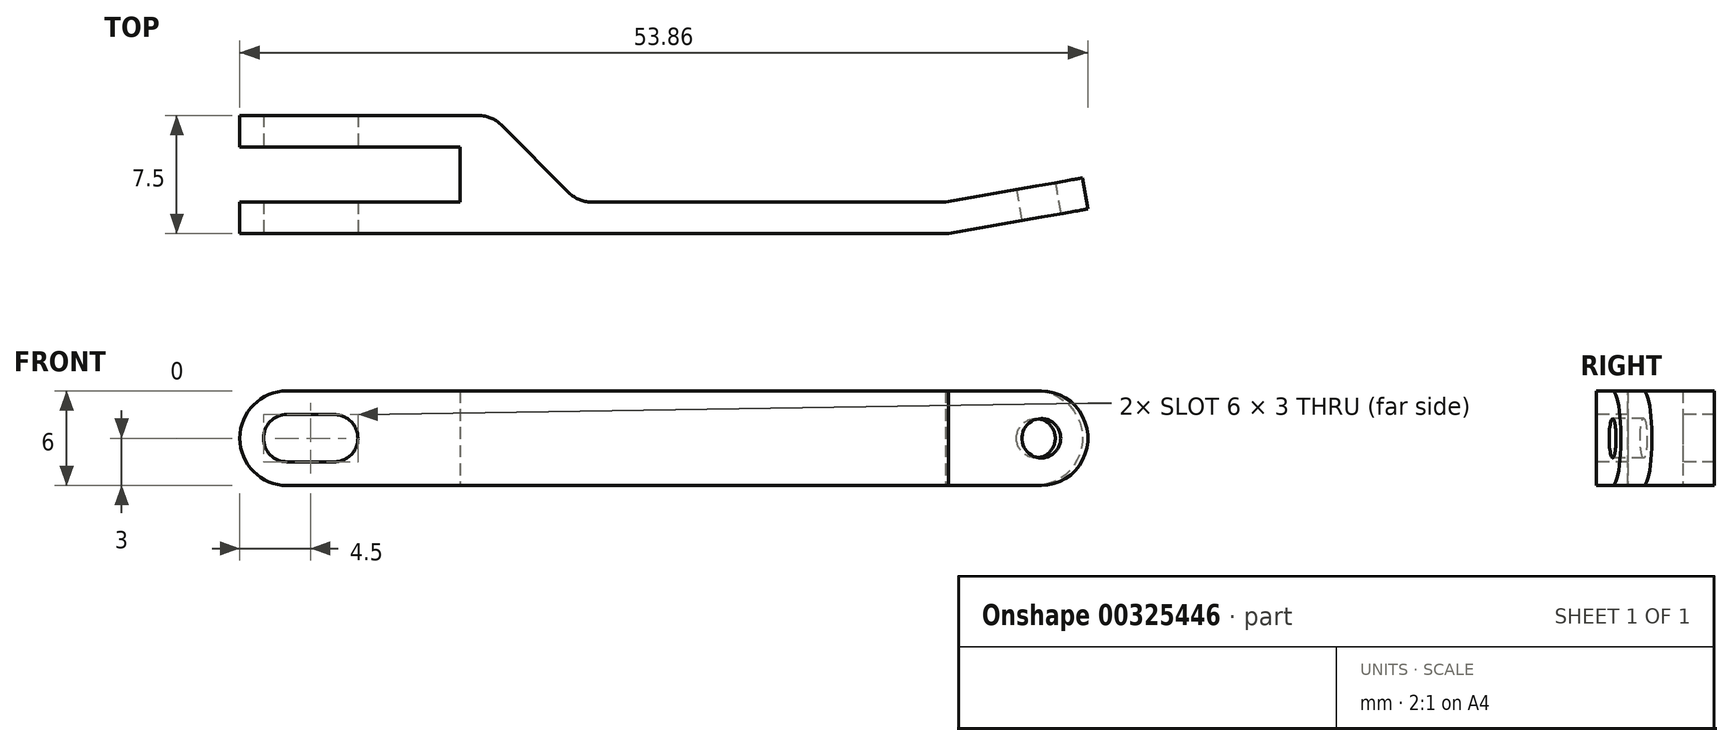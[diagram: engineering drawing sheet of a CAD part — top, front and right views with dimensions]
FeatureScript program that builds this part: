
annotation { "Feature Type Name" : "Feature", "Feature Type Description" : "" }
export const myFeature = defineFeature(function(context is Context, id is Id, definition is map)
    precondition{}
    {
        {
            var Q0;
            Q0=qCreatedBy(makeId("Top.planeOp"),FACE);
            var sketch = newSketch(context, id + "F0", { "sketchPlane" : qUnion([Q0])});
            skLineSegment(sketch, "E0.bottom", {"start": v(22.5, -1) * mm, "end": v(-22.5, -1) * mm});
            skLineSegment(sketch, "E0.top", {"start": v(22.5, 1) * mm, "end": v(-0.17, 1) * mm});
            skLineSegment(sketch, "E0.right", {"start": v(-22.5, -1) * mm, "end": v(-22.5, 1) * mm});
            skPoint(sketch, "E0.middle", {"position": v(0, 0) * mm});
            skLineSegment(sketch, "E1", {"start": v(22.5, -1) * mm, "end": v(31.36, 0.56) * mm});
            skLineSegment(sketch, "E2.0", {"start": v(22.15, 0.97) * mm, "end": v(31.02, 2.53) * mm});
            skLineSegment(sketch, "E3", {"start": v(31.02, 2.53) * mm, "end": v(31.36, 0.56) * mm});
            skLineSegment(sketch, "E4.0", {"start": v(-8.5, 4.5) * mm, "end": v(-22.5, 4.5) * mm});
            skLineSegment(sketch, "E5", {"start": v(-8.5, 4.5) * mm, "end": v(-8.5, 1) * mm});
            skLineSegment(sketch, "E6.0", {"start": v(-7.33, 6.5) * mm, "end": v(-22.5, 6.5) * mm});
            skLineSegment(sketch, "E7", {"start": v(-22.5, 6.5) * mm, "end": v(-22.5, 4.5) * mm});
            skLineSegment(sketch, "E8", {"start": v(-5.91, 5.91) * mm, "end": v(-1.59, 1.59) * mm});
            skPoint(sketch, "E9.visualSharp", {"position": v(-6.5, 6.5) * mm});
            skArc(sketch, "E9.filletArc", {"start": v(-5.91, 5.91) * mm, "mid": v(-6.56, 6.35) * mm, "end": v(-7.33, 6.5) * mm});
            skPoint(sketch, "E10.newPointB", {"position": v(-22.5, 1) * mm});
            skArc(sketch, "E10.filletArc", {"start": v(-1.59, 1.59) * mm, "mid": v(-0.94, 1.15) * mm, "end": v(-0.17, 1) * mm});
            skLineSegment(sketch, "E11", {"start": v(-22.5, 1) * mm, "end": v(-8.5, 1) * mm});
            skSolve(sketch);
        }
        {
            var Q0;
            Q0=makeQuery(id+"F0.imprint","IMPRINT",FACE,{"disambiguationData":[TD([[makeQuery(id+"F0.imprint","IMPRINT",EDGE,{"derivedFrom":sQuery(id+"F0.wireOp",EDGE,"E0.bottom")}),-1.0]])]});
            extrude(context, id + "F1", {"entities" : qUnion([Q0]), "depth" : 6 * mm});
        }
        {
            var Q0;
            Q0=makeQuery(id+"F1.opExtrude","SWEPT_FACE",FACE,{"disambiguationData":[OSD([sQuery(id+"F0.wireOp",EDGE,"E0.bottom")])]});
            var sketch = newSketch(context, id + "F2", { "sketchPlane" : qUnion([Q0])});
            skArc(sketch, "E12", {"start": v(-19.5, 4.5) * mm, "mid": v(-21, 3) * mm, "end": v(-19.5, 1.5) * mm});
            skArc(sketch, "E13", {"start": v(-16.5, 1.5) * mm, "mid": v(-15, 3) * mm, "end": v(-16.5, 4.5) * mm});
            skLineSegment(sketch, "E14", {"start": v(-19.5, 4.5) * mm, "end": v(-16.5, 4.5) * mm});
            skLineSegment(sketch, "E15", {"start": v(-16.5, 1.5) * mm, "end": v(-19.5, 1.5) * mm});
            skSolve(sketch);
        }
        {
            var Q0;
            Q0=makeQuery(id+"F2.imprint","IMPRINT",FACE,{"disambiguationData":[TD([[makeQuery(id+"F2.imprint","IMPRINT",EDGE,{"derivedFrom":sQuery(id+"F2.wireOp",EDGE,"E12")}),1.0]])]});
            extrude(context, id + "F3", {"entities" : qUnion([Q0]), "operationType" : NewBodyOperationType.REMOVE, "oppositeDirection" : true, "depth" : 25 * mm});
        }
        {
            var Q0;
            Q0=makeQuery(id+"F1.opExtrude","CAP_EDGE",EDGE,{"disambiguationData":[OSD([sQuery(id+"F0.wireOp",EDGE,"E7")])],"isStart":false});
            var Q1;
            Q1=makeQuery(id+"F1.opExtrude","CAP_EDGE",EDGE,{"disambiguationData":[OSD([sQuery(id+"F0.wireOp",EDGE,"E0.right")])],"isStart":false});
            var Q2;
            Q2=makeQuery(id+"F1.opExtrude","CAP_EDGE",EDGE,{"disambiguationData":[OSD([sQuery(id+"F0.wireOp",EDGE,"E7")])],"isStart":true});
            var Q3;
            Q3=makeQuery(id+"F1.opExtrude","CAP_EDGE",EDGE,{"disambiguationData":[OSD([sQuery(id+"F0.wireOp",EDGE,"E0.right")])],"isStart":true});
            fillet(context, id + "F4", {"entities" : qUnion([Q0, Q1, Q2, Q3]), "radius" : 3 * mm, "tangentPropagation" : true, "allowEdgeOverflow" : false});
        }
        {
            var Q0;
            Q0=makeQuery(id+"F1.opExtrude","SWEPT_FACE",FACE,{"disambiguationData":[OSD([sQuery(id+"F0.wireOp",EDGE,"E1")])]});
            var sketch = newSketch(context, id + "F5", { "sketchPlane" : qUnion([Q0])});
            skCircle(sketch, "E16", {"center": v(27.98, 3) * mm, "radius": 1.25 * mm});
            skPoint(sketch, "E16.centerSnap0", {"position": v(30.98, 3) * mm});
            skSolve(sketch);
        }
        {
            var Q0;
            Q0=makeQuery(id+"F5.imprint","IMPRINT",FACE,{"disambiguationData":[TD([[makeQuery(id+"F5.imprint","IMPRINT",EDGE,{"derivedFrom":sQuery(id+"F5.wireOp",EDGE,"E16")}),1.0]])]});
            extrude(context, id + "F6", {"entities" : qUnion([Q0]), "operationType" : NewBodyOperationType.REMOVE, "oppositeDirection" : true, "depth" : 25 * mm});
        }
        {
            var Q0;
            Q0=makeQuery(id+"F1.opExtrude","CAP_EDGE",EDGE,{"disambiguationData":[OSD([sQuery(id+"F0.wireOp",EDGE,"E3")])],"isStart":false});
            var Q1;
            Q1=makeQuery(id+"F1.opExtrude","CAP_EDGE",EDGE,{"disambiguationData":[OSD([sQuery(id+"F0.wireOp",EDGE,"E3")])],"isStart":true});
            fillet(context, id + "F7", {"entities" : qUnion([Q0, Q1]), "radius" : 3 * mm, "tangentPropagation" : true, "allowEdgeOverflow" : false});
        }
    });
